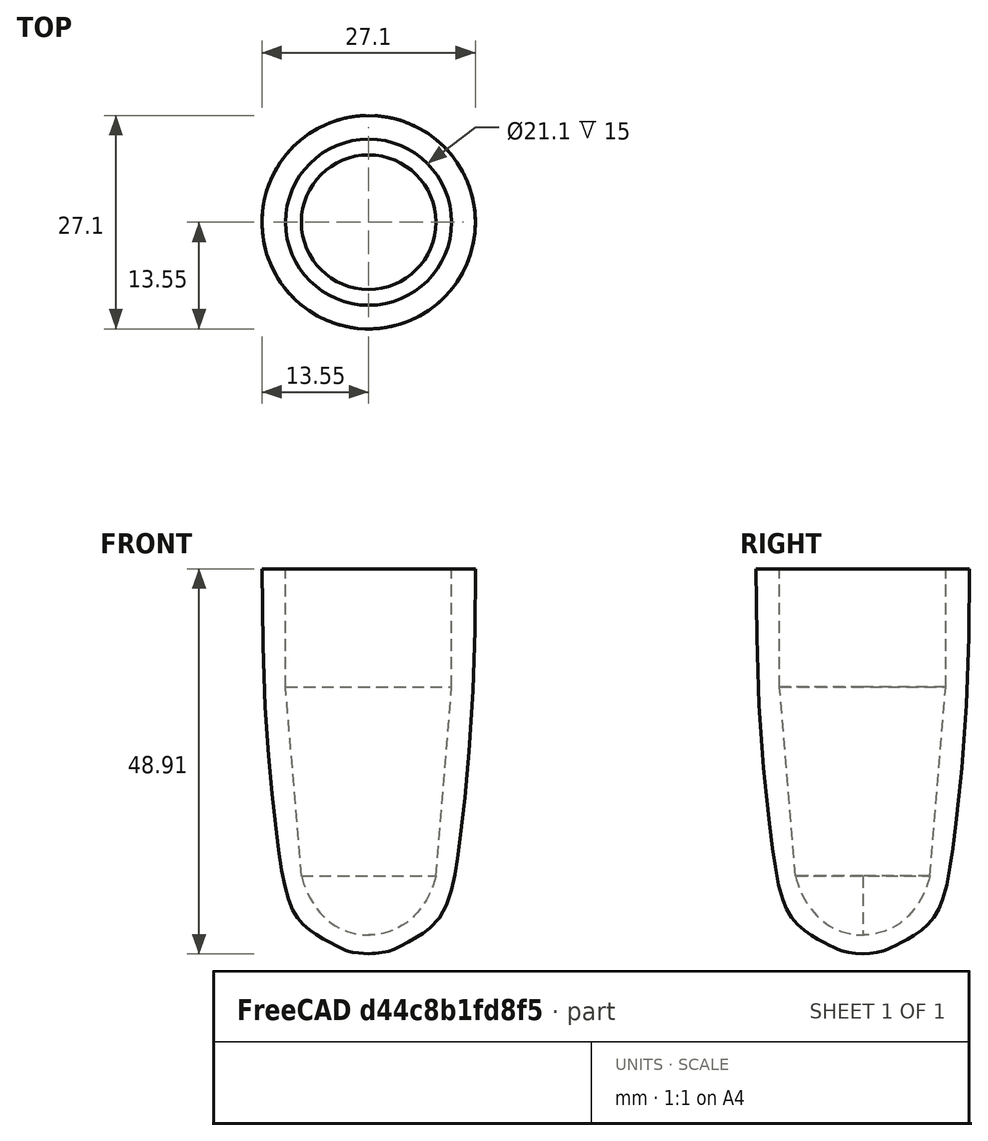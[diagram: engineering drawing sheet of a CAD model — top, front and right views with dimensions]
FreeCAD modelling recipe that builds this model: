
FCSTD DOCUMENT  (FreeCAD 2024.2R37179 (Git))
Label: Walking-Stick-Rubber
License: All rights reserved
LicenseURL: https://en.wikipedia.org/wiki/All_rights_reserved
objects: Sketcher::SketchObject×1, App::VarSet×1, PartDesign::Revolution×1, PartDesign::Body×1
note: 4 computed .brp shape members not serialized (recipe doc carries the construction recipe); baked Part::Feature solids carry a one-line shape summary decoded from their .brp

FEATURE [Sketcher::SketchObject] Sketch
  AttachmentSupport = -> [XZ_Plane]
  FullyConstrained = false
  MapMode = 5
  Placement = pos=(0,0,0) rot=(1,0,0;1.5708rad)
  expr: Constraints[1] = 10.55
  expr: Constraints[2] = 8.55
  sketch-geometry (26):
    g0: LineSegment StartX=-8.55 StartY=0 StartZ=0 EndX=-10.55 EndY=24 EndZ=0
    g1-g4: Circle x4 (B-spline internal-alignment scaffolding for g5; pole/knot coordinates omitted)
    g5: BSplineCurve PolesCount=4 KnotsCount=2 Degree=3 IsPeriodic=0
    g6: GeomPoint X=-8.55 Y=0 Z=0
    g7: GeomPoint X=0 Y=-7.5 Z=0
    g8: LineSegment StartX=-10.55 StartY=24 StartZ=0 EndX=-10.55 EndY=39 EndZ=0
    g9: LineSegment StartX=-10.55 StartY=39 StartZ=0 EndX=-13.55 EndY=39 EndZ=0
    g10-g17: Circle x8 (B-spline internal-alignment scaffolding for g18; pole/knot coordinates omitted)
    g18: BSplineCurve PolesCount=8 KnotsCount=6 Degree=3 IsPeriodic=0
    g19-g24: GeomPoint x6 (B-spline internal-alignment scaffolding for g18; pole/knot coordinates omitted)
    g25: LineSegment StartX=0 StartY=-9.90565 StartZ=0 EndX=0 EndY=-7.5 EndZ=0
  constraints (31):
    c: PointOnObject(g0,g-1)
    c: Distance(g0,g-2) = 10.55
    c: DistanceX(g0,g-1) = 8.55
    c: DistanceY(g-1,g0) = 24
    c: Weight(g1) = 1
    c: Coincident(g5,g0)
    c: Equal(g1,g2)
    c: Equal(g1,g3)
    c: Equal(g1,g4)
    c: Coincident(g5,g3)
    c: InternalAlignment(g1-g4 -> g5) x4
    c: InternalAlignment(g6,g5)
    c: InternalAlignment(g7,g5)
    c: PointOnObject(g4,g-2)
    c: DistanceY(g4,g-1) = 7.5
    c: Coincident(g0,g8)
    c: Vertical(g8)
    c: DistanceY(g8,g8) = 15
    c: Coincident(g8,g9)
    c: Horizontal(g9)
    c: DistanceX(g9,g9) = 3
    c: Weight(g10) = 1
    c: Coincident(g18,g9)
    c: Equal(g10, g11-g16) x6
    c: Coincident(g16,g15)
    c: Equal(g10,g17)
    c: InternalAlignment(g10-g17 -> g18) x8
    c: InternalAlignment(g19-g24 -> g18) x6
    c: Coincident(g25,g18)
    c: Coincident(g25,g4)
    c: Vertical(g25)
FEATURE [App::VarSet] VarSet
  Settings = 8.55
FEATURE [PartDesign::Revolution] Revolution
  Angle = 360
  Angle2 = 60
  Axis = (0,2e-16,1)
  Base = (0,0,0)
  Placement = pos=(0,0,0) rot=(1,0,0;1.5708rad)
  Profile = -> Sketch
  ReferenceAxis = -> Sketch [V_Axis]
  Refine = true
  Suppressed = false
  Type = 0
FEATURE [PartDesign::Body] Body
  Group = -> [Sketch,Revolution]
  Origin = -> Origin
  Tip = -> Revolution
